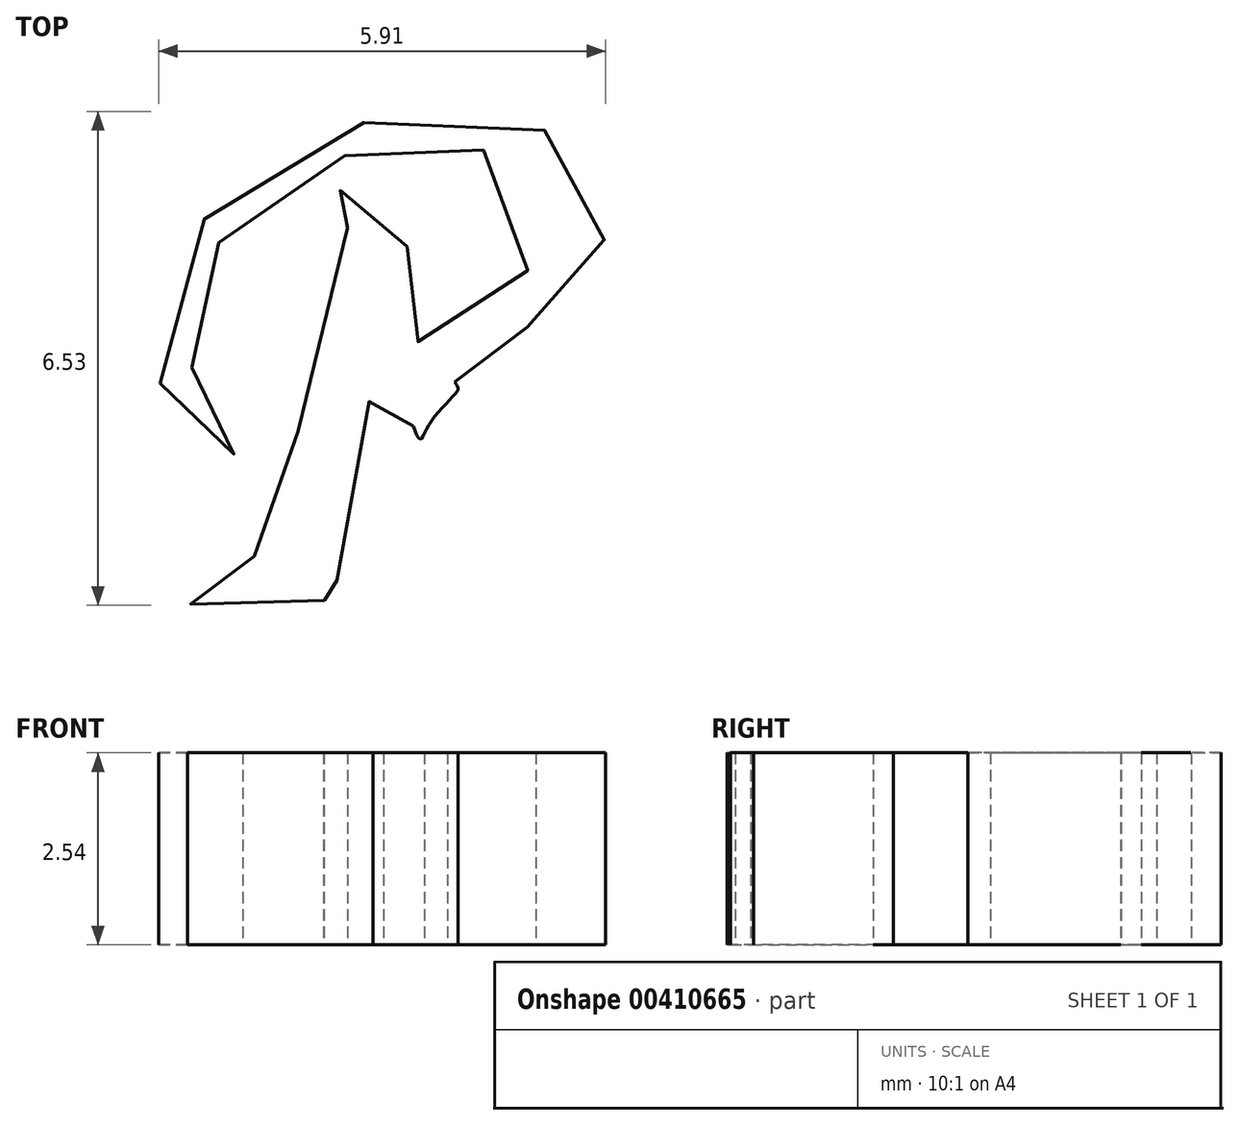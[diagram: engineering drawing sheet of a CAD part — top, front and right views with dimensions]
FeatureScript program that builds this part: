
annotation { "Feature Type Name" : "Feature", "Feature Type Description" : "" }
export const myFeature = defineFeature(function(context is Context, id is Id, definition is map)
    precondition{}
    {
        {
            var Q0;
            Q0=qCreatedBy(makeId("Top.planeOp"),FACE);
            var sketch = newSketch(context, id + "F0", { "sketchPlane" : qUnion([Q0])});
            skPoint(sketch, "E0.middle", {"position": v(0, 0) * mm});
            skFitSpline(sketch, "E1", {"points": [v(-4.04, 0.72) * mm, v(-3.8, 0.67) * mm, v(-3.6, 0.79) * mm, v(-3.57, 1.09) * mm, v(-3.84, 1.35) * mm, v(-4.12, 1.67) * mm, v(-4.29, 2.18) * mm, v(-4.24, 2.7) * mm, v(-4.02, 3.28) * mm, v(-3.62, 3.8) * mm, v(-3, 4.3) * mm, v(-2.2, 4.67) * mm, v(-1.44, 4.84) * mm, v(-0.88, 4.86) * mm, v(-0.27, 4.7) * mm, v(0.25, 4.2) * mm, v(0.3, 3.52) * mm, v(0.12, 2.96) * mm, v(-0.44, 2.41) * mm, v(-0.94, 2.23) * mm, v(-1.46, 2.23) * mm, v(-1.68, 2.26) * mm, v(-1.67, 2.39) * mm, v(-1.46, 3.14) * mm, v(-1.14, 4.4) * mm, v(-1.15, 4.4) * mm, v(-1.83, 4.25) * mm, v(-2.41, 4.2) * mm, v(-2.42, 4.19) * mm, v(-2.48, 3.95) * mm, v(-2.46, 3.94) * mm, v(-2.29, 3.93) * mm, v(-2.2, 3.9) * mm, v(-2.17, 3.78) * mm, v(-2.2, 3.48) * mm, v(-2.55, 2.06) * mm, v(-3.04, 0.13) * mm, v(-3.13, -0.19) * mm, v(-3.27, -0.44) * mm, v(-3.43, -0.65) * mm, v(-3.83, -0.84) * mm, v(-4.18, -0.95) * mm, v(-4.21, -0.98) * mm, v(-4.27, -1.26) * mm, v(-4.22, -1.25) * mm, v(-3.73, -1.18) * mm, v(-3.01, -1.16) * mm, v(-2.38, -1.2) * mm, v(-1.85, -1.2) * mm, v(-1.83, -1.17) * mm, v(-1.84, -0.93) * mm, v(-1.93, -0.94) * mm, v(-2.46, -0.92) * mm, v(-2.47, -0.88) * mm, v(-2.07, 0.65) * mm, v(-1.76, 1.87) * mm, v(-1.73, 1.92) * mm, v(-1.52, 1.9) * mm, v(-1.45, 1.78) * mm, v(-1.22, 0.93) * mm, v(-1.08, 1.13) * mm, v(-0.7, 1.57) * mm, v(-0.72, 1.64) * mm, v(-0.84, 1.9) * mm, v(-0.7, 1.91) * mm, v(-0.24, 2.05) * mm, v(0.16, 2.37) * mm, v(0.76, 2.7) * mm, v(0.9, 2.81) * mm, v(1.15, 3.24) * mm, v(1.25, 3.86) * mm, v(1.16, 4.31) * mm, v(0.79, 4.8) * mm, v(0, 5.17) * mm, v(-0.98, 5.26) * mm, v(-2.44, 4.97) * mm, v(-3.58, 4.34) * mm, v(-4.16, 3.7) * mm, v(-4.58, 2.84) * mm, v(-4.64, 1.71) * mm, v(-4.5, 1.24) * mm, v(-4.04, 0.72) * mm]});
            skFitSpline(sketch, "E2", {"points": [v(-0.1, 0.11) * mm, v(0.13, -0.39) * mm, v(0.34, -0.76) * mm, v(0.52, -0.97) * mm, v(0.7, -1.13) * mm, v(1.13, -1.36) * mm, v(1.57, -1.36) * mm, v(1.9, -1.14) * mm, v(2.07, -0.73) * mm, v(2.15, -0.56) * mm, v(2.24, -0.48) * mm, v(2.5, -0.47) * mm, v(2.68, -0.65) * mm, v(2.67, -0.97) * mm, v(2.5, -1.27) * mm, v(2.2, -1.53) * mm, v(1.78, -1.67) * mm, v(1.44, -1.7) * mm, v(0.82, -1.62) * mm, v(0.22, -1.33) * mm, v(-0.26, -0.92) * mm, v(-0.34, -0.82) * mm, v(-0.22, -0.17) * mm, v(-0.12, 0.1) * mm, v(-0.1, 0.11) * mm]});
            skFitSpline(sketch, "E3", {"points": [v(4.12, 0.72) * mm, v(4.13, 1.25) * mm, v(4.22, 1.87) * mm, v(4.39, 2.57) * mm, v(4.34, 2.58) * mm, v(3.49, 2.68) * mm, v(3.07, 2.79) * mm, v(2.2, 2.87) * mm, v(1.16, 2.62) * mm, v(-0.1, 1.86) * mm, v(-1.23, 0.33) * mm, v(-1.6, -1.2) * mm, v(-1.37, -2.53) * mm, v(-0.8, -3.24) * mm, v(0.22, -3.66) * mm, v(1.46, -3.55) * mm, v(2.03, -3.28) * mm, v(2, -3.45) * mm, v(1.72, -4.24) * mm, v(1.43, -4.77) * mm, v(1.09, -5.07) * mm, v(0.64, -5.13) * mm, v(0.22, -4.84) * mm, v(-0.1, -4.5) * mm, v(-0.31, -4.4) * mm, v(-0.58, -4.5) * mm, v(-0.7, -4.8) * mm, v(-0.52, -5.15) * mm, v(-0.13, -5.43) * mm, v(0.37, -5.53) * mm, v(0.9, -5.48) * mm, v(1.35, -5.36) * mm, v(1.94, -4.97) * mm, v(2.57, -4.12) * mm, v(2.97, -2.95) * mm, v(3.19, -2.05) * mm, v(3.3, -1.67) * mm, v(3.37, -1.55) * mm, v(3.52, -1.43) * mm, v(3.77, -1.42) * mm, v(3.78, -1.39) * mm, v(3.82, -1.14) * mm, v(3.77, -1.14) * mm, v(3.22, -1.17) * mm, v(2.86, -1.18) * mm, v(2.84, -1.2) * mm, v(2.72, -1.39) * mm, v(2.59, -1.53) * mm, v(2.43, -1.65) * mm, v(2.41, -1.7) * mm, v(2.38, -2.02) * mm, v(2.25, -2.56) * mm, v(2.17, -2.85) * mm, v(2.1, -2.9) * mm, v(1.57, -3.12) * mm, v(1.02, -3.2) * mm, v(0.63, -3.18) * mm, v(0.22, -3.03) * mm, v(-0.2, -2.7) * mm, v(-0.37, -2.45) * mm, v(-0.52, -2.13) * mm, v(-0.64, -1.56) * mm, v(-0.61, -0.82) * mm, v(-0.5, -0.2) * mm, v(-0.07, 0.79) * mm, v(0.35, 1.37) * mm, v(0.83, 1.84) * mm, v(1.43, 2.23) * mm, v(1.9, 2.44) * mm, v(2.5, 2.51) * mm, v(2.93, 2.48) * mm, v(3.39, 2.27) * mm, v(3.65, 1.98) * mm, v(3.8, 1.57) * mm, v(3.8, 0.72) * mm, v(3.81, 0.7) * mm, v(4.04, 0.7) * mm, v(4.11, 0.7) * mm, v(4.12, 0.72) * mm]});
            skArc(sketch, "E4", {"start": v(-1.3, 1.1) * mm, "mid": v(-1.21, 0.83) * mm, "end": v(-1.12, 0.55) * mm});
            skArc(sketch, "E5", {"start": v(-0.56, 1.37) * mm, "mid": v(-0.65, 1.53) * mm, "end": v(-0.75, 1.68) * mm});
            skArc(sketch, "E6", {"start": v(-0.58, -0.58) * mm, "mid": v(-0.38, -0.82) * mm, "end": v(-0.13, -1.03) * mm});
            skArc(sketch, "E7", {"start": v(-0.21, 0.52) * mm, "mid": v(-0.15, 0.27) * mm, "end": v(-0.05, 0.03) * mm});
            skSolve(sketch);
        }
        {
            var Q0;
            Q0=makeQuery(id+"F0.imprint","IMPRINT",FACE,{"disambiguationData":[TD([[makeQuery(id+"F0.imprint","IMPRINT",EDGE,{"derivedFrom":sQuery(id+"F0.wireOp",EDGE,"E1")}),1.0]])]});
            extrude(context, id + "F1", {"entities" : qUnion([Q0]), "depth" : 2.54 * mm});
        }
    });
